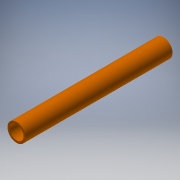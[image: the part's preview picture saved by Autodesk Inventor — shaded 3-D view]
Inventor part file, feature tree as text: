
AUTODESK INVENTOR PART (.ipt)
format: ipt  version: 2018 (Build 220112000, 112)  size: 108,032 bytes
history: native  units: in
note: dims shown in document units (in); Inventor stores cm internally (conversion verified against a paired STEP export)
features: extrude x1, sketch x1
ambient origin geometry x8: Origin, YZ Plane, XZ Plane, XY Plane, X Axis, Y Axis, Z Axis, Center Point
bodies: Solid1 (feature_tree)
feature tree (2):
  extrude  "Extrusion1"  Depth=10.584in
  sketch  "Sketch1"  dims[d0=1.315in d1=1.0in d2=10.584in d3=0.0in]
